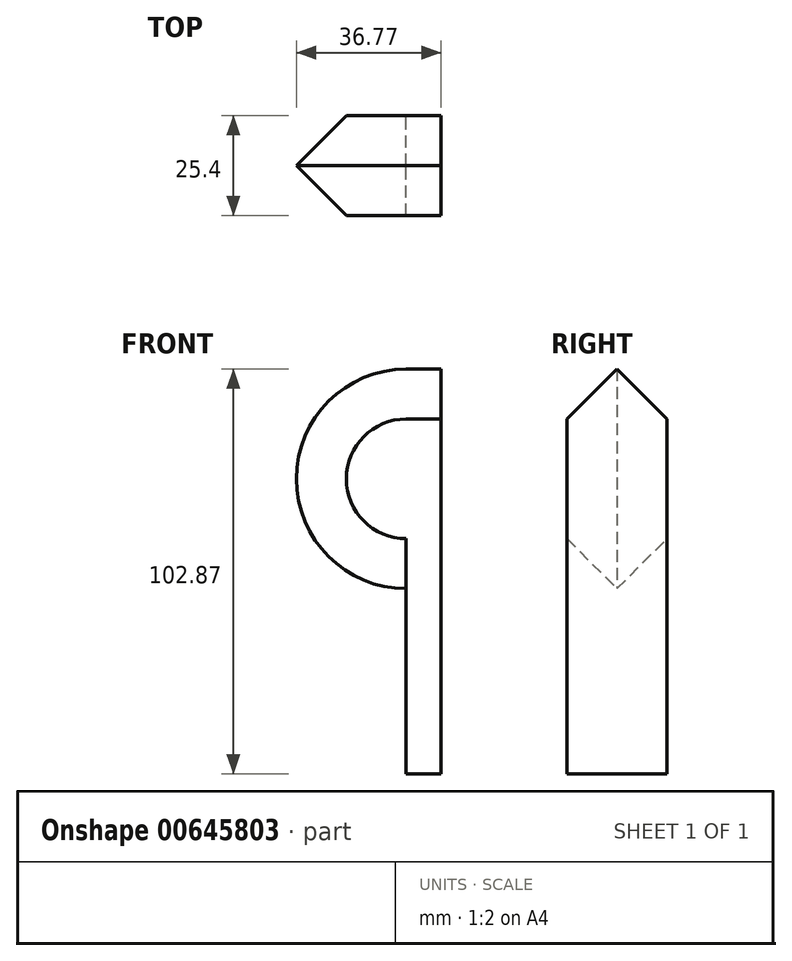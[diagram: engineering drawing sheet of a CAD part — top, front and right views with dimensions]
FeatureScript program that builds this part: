
annotation { "Feature Type Name" : "Feature", "Feature Type Description" : "" }
export const myFeature = defineFeature(function(context is Context, id is Id, definition is map)
    precondition{}
    {
        {
            var Q0;
            Q0=qCreatedBy(makeId("Front.planeOp"),FACE);
            var sketch = newSketch(context, id + "F0", { "sketchPlane" : qUnion([Q0])});
            skArc(sketch, "E0", {"start": v(0, 55.8) * mm, "mid": v(-27.9, 27.9) * mm, "end": v(0, 0) * mm});
            skLineSegment(sketch, "E1", {"start": v(0, 0) * mm, "end": v(0, -47.07) * mm});
            skLineSegment(sketch, "E2", {"start": v(0, -47.07) * mm, "end": v(8.87, -47.07) * mm});
            skLineSegment(sketch, "E3", {"start": v(8.87, -47.07) * mm, "end": v(8.87, 55.8) * mm});
            skLineSegment(sketch, "E4", {"start": v(8.87, 55.8) * mm, "end": v(0, 55.8) * mm});
            skSolve(sketch);
        }
        {
            var Q0;
            Q0 = qSketchRegion(id + "F0", true);
            extrude(context, id + "F1", {"entities" : qUnion([Q0]), "depth" : 25.4 * mm, "offsetDistance" : 25.4 * mm});
        }
        {
            var Q0;
            Q0=makeQuery(id+"F1.opExtrude","CAP_EDGE",EDGE,{"disambiguationData":[OSD([sQuery(id+"F0.wireOp",EDGE,"E0")])],"isStart":false});
            var Q1;
            Q1=makeQuery(id+"F1.opExtrude","CAP_EDGE",EDGE,{"disambiguationData":[OSD([sQuery(id+"F0.wireOp",EDGE,"E0")])],"isStart":true});
            chamfer(context, id + "F2", {"entities" : qUnion([Q0, Q1]), "width" : 12.7 * mm, "tangentPropagation" : true});
        }
    });
